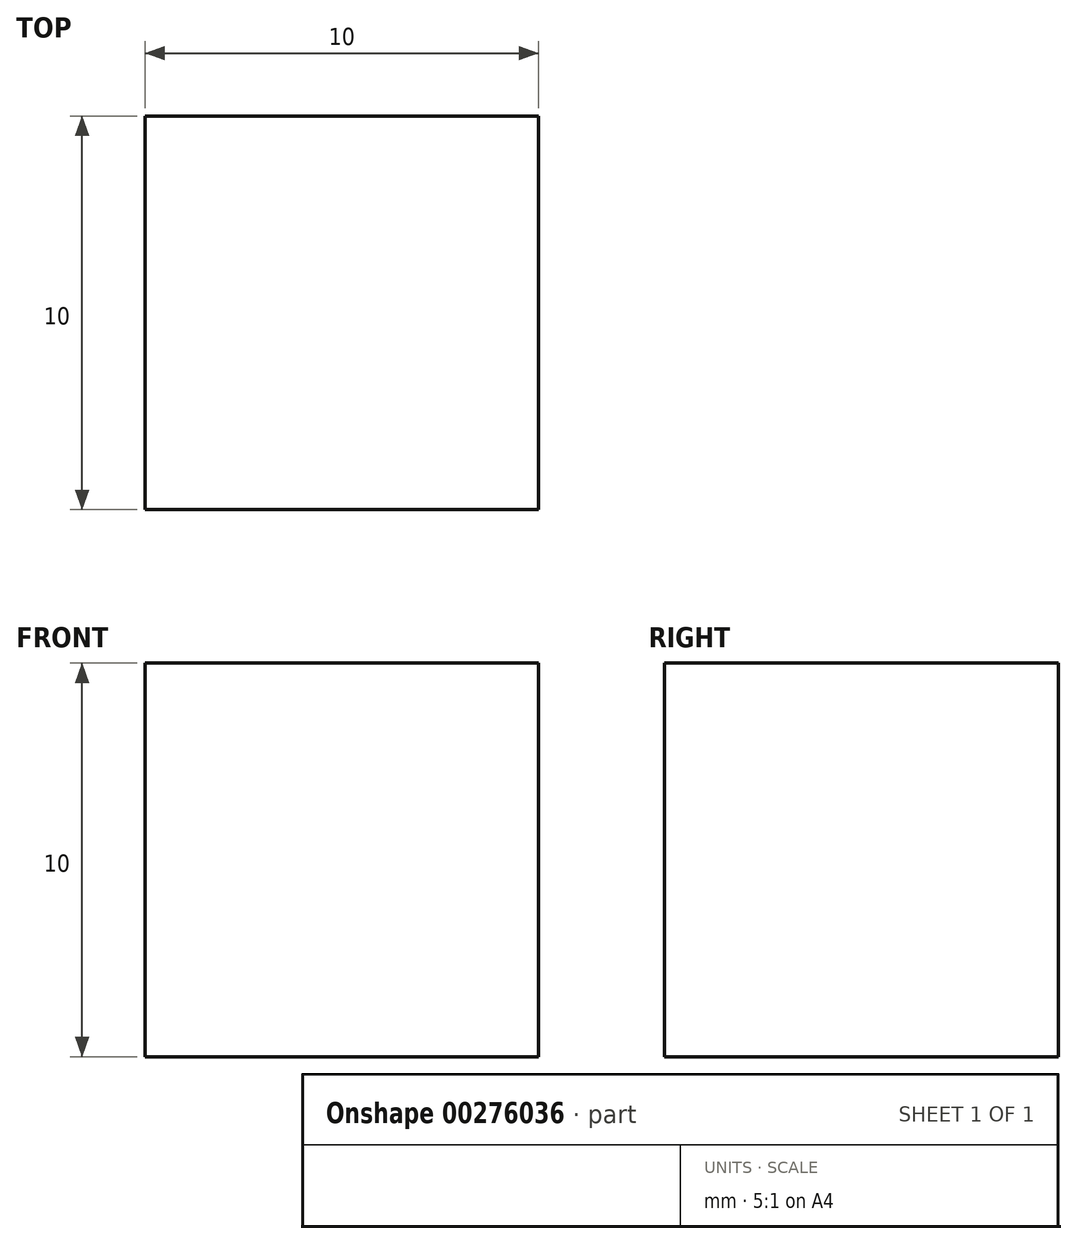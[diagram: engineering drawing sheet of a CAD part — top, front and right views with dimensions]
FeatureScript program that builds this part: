
annotation { "Feature Type Name" : "Feature", "Feature Type Description" : "" }
export const myFeature = defineFeature(function(context is Context, id is Id, definition is map)
    precondition{}
    {
        {
            var Q0;
            Q0=qCreatedBy(makeId("Top.planeOp"),FACE);
            var sketch = newSketch(context, id + "F0", { "sketchPlane" : qUnion([Q0])});
            skLineSegment(sketch, "E0.bottom", {"start": v(-10.74, 0) * mm, "end": v(-0.74, 0) * mm});
            skLineSegment(sketch, "E0.top", {"start": v(-10.74, -10) * mm, "end": v(-0.74, -10) * mm});
            skLineSegment(sketch, "E0.left", {"start": v(-10.74, 0) * mm, "end": v(-10.74, -10) * mm});
            skLineSegment(sketch, "E0.right", {"start": v(-0.74, 0) * mm, "end": v(-0.74, -10) * mm});
            skSolve(sketch);
        }
        {
            var Q0;
            Q0 = qSketchRegion(id + "F0", true);
            extrude(context, id + "F1", {"entities" : qUnion([Q0]), "depth" : 10 * mm});
        }
    });
